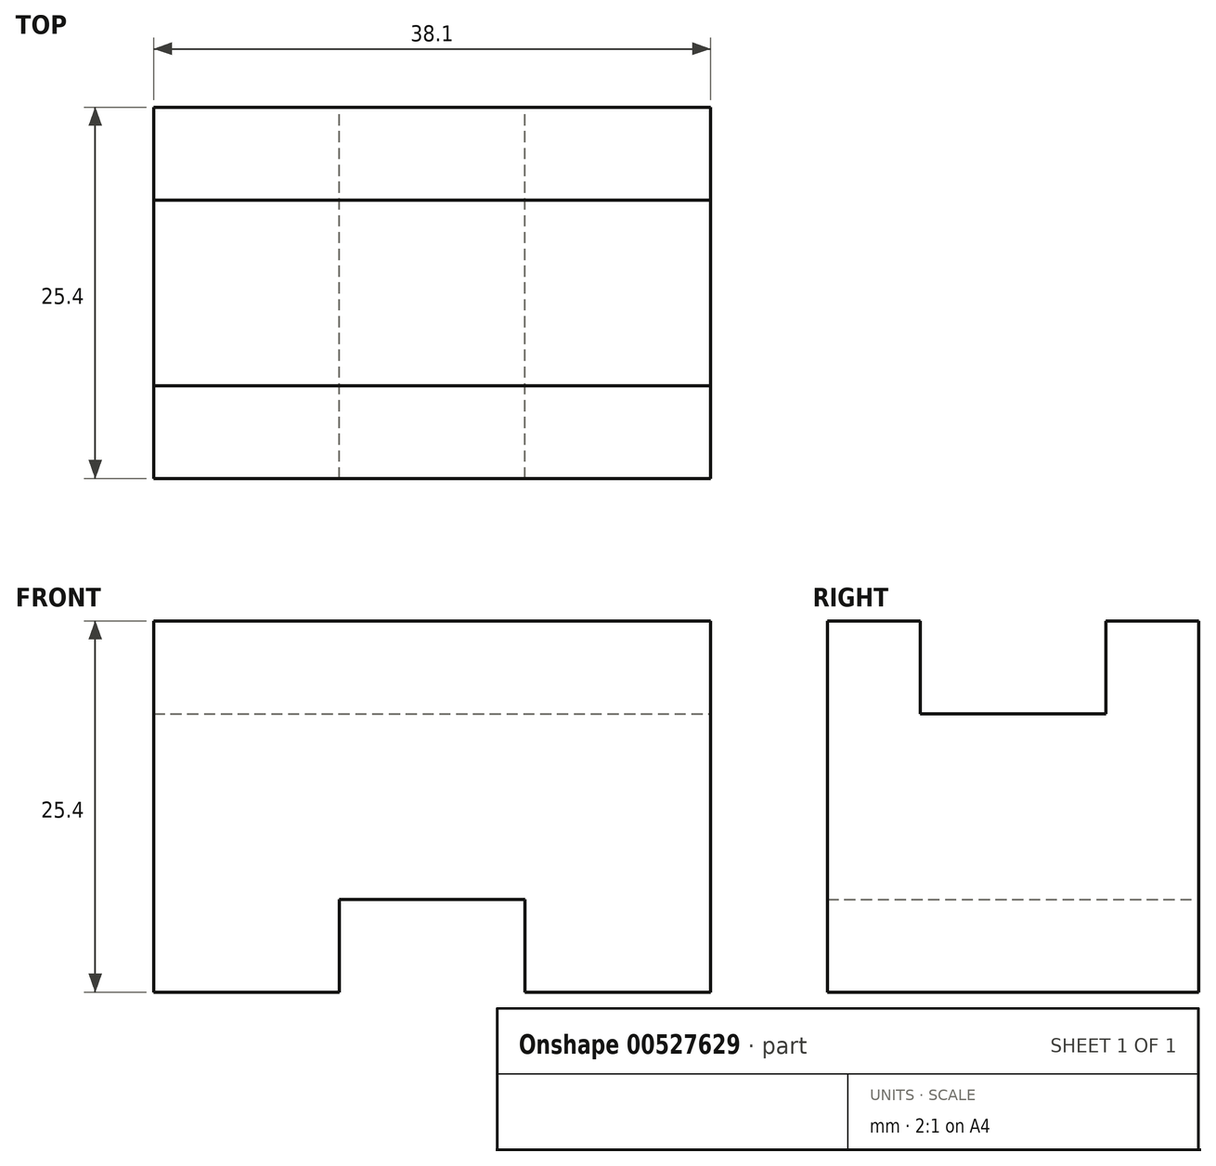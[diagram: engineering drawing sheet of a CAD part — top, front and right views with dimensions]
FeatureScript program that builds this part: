
annotation { "Feature Type Name" : "Feature", "Feature Type Description" : "" }
export const myFeature = defineFeature(function(context is Context, id is Id, definition is map)
    precondition{}
    {
        {
            var Q0;
            Q0=qCreatedBy(makeId("Front.planeOp"),FACE);
            var sketch = newSketch(context, id + "F0", { "sketchPlane" : qUnion([Q0])});
            skLineSegment(sketch, "E0", {"start": v(0, 0) * mm, "end": v(38.1, 0) * mm});
            skLineSegment(sketch, "E1", {"start": v(38.1, 0) * mm, "end": v(38.1, 25.4) * mm});
            skLineSegment(sketch, "E2", {"start": v(0, 25.4) * mm, "end": v(38.1, 25.4) * mm});
            skLineSegment(sketch, "E3", {"start": v(0, 25.4) * mm, "end": v(0, 0) * mm});
            skSolve(sketch);
        }
        {
            var Q0;
            Q0 = qSketchRegion(id + "F0", true);
            extrude(context, id + "F1", {"entities" : qUnion([Q0]), "depth" : 25.4 * mm, "offsetDistance" : 25.4 * mm});
        }
        {
            var Q0;
            Q0=makeQuery(id+"F1.opExtrude","SWEPT_FACE",FACE,{"disambiguationData":[OSD([sQuery(id+"F0.wireOp",EDGE,"E2")])]});
            var sketch = newSketch(context, id + "F2", { "sketchPlane" : qUnion([Q0])});
            skLineSegment(sketch, "E4", {"start": v(0, -6.35) * mm, "end": v(38.1, -6.35) * mm});
            skLineSegment(sketch, "E5", {"start": v(0, -19.05) * mm, "end": v(38.1, -19.05) * mm});
            skSolve(sketch);
        }
        {
            var Q0;
            {var subQ0=sQuery(id+"F2.wireOp",EDGE,"E4");Q0=makeQuery(id+"F2.imprint","IMPRINT",FACE,{"disambiguationData":[TD([[makeQuery(id+"F2.imprint","IMPRINT",EDGE,{"derivedFrom":subQ0}),-1.0]])]});}
            extrude(context, id + "F3", {"entities" : qUnion([Q0]), "operationType" : NewBodyOperationType.REMOVE, "oppositeDirection" : true, "depth" : 6.35 * mm, "offsetDistance" : 25.4 * mm});
        }
        {
            var Q0;
            {var subQ0=sQuery(id+"F2.wireOp",EDGE,"E4");Q0=makeQuery(id+"F2.imprint","IMPRINT",FACE,{"disambiguationData":[TD([[makeQuery(id+"F2.imprint","IMPRINT",EDGE,{"derivedFrom":subQ0}),-1.0]])]});}
            extrude(context, id + "F4", {"entities" : qUnion([Q0]), "operationType" : NewBodyOperationType.REMOVE, "oppositeDirection" : true, "depth" : 6.35 * mm, "offsetDistance" : 25.4 * mm});
        }
        {
            var Q0;
            Q0=makeQuery(id+"F1.opExtrude","SWEPT_FACE",FACE,{"disambiguationData":[OSD([sQuery(id+"F0.wireOp",EDGE,"E0")])]});
            var sketch = newSketch(context, id + "F5", { "sketchPlane" : qUnion([Q0])});
            skLineSegment(sketch, "E6", {"start": v(25.4, 25.4) * mm, "end": v(25.4, 0) * mm});
            skLineSegment(sketch, "E7.0.0", {"start": v(0, 0) * mm, "end": v(38.1, 0) * mm});
            skLineSegment(sketch, "E7.0.1", {"start": v(38.1, 0) * mm, "end": v(38.1, 25.4) * mm});
            skLineSegment(sketch, "E7.0.2", {"start": v(38.1, 25.4) * mm, "end": v(0, 25.4) * mm});
            skLineSegment(sketch, "E7.0.3", {"start": v(0, 25.4) * mm, "end": v(0, 0) * mm});
            skLineSegment(sketch, "E8", {"start": v(12.7, 25.4) * mm, "end": v(12.7, 0) * mm});
            skSolve(sketch);
        }
        {
            var Q0;
            {var subQ0=sQuery(id+"F5.wireOp",EDGE,"E6");Q0=makeQuery(id+"F5.imprint","IMPRINT",FACE,{"disambiguationData":[TD([[makeQuery(id+"F5.imprint","IMPRINT",EDGE,{"derivedFrom":subQ0}),-1.0]])]});}
            extrude(context, id + "F6", {"entities" : qUnion([Q0]), "operationType" : NewBodyOperationType.REMOVE, "oppositeDirection" : true, "depth" : 6.35 * mm, "offsetDistance" : 25.4 * mm});
        }
    });
